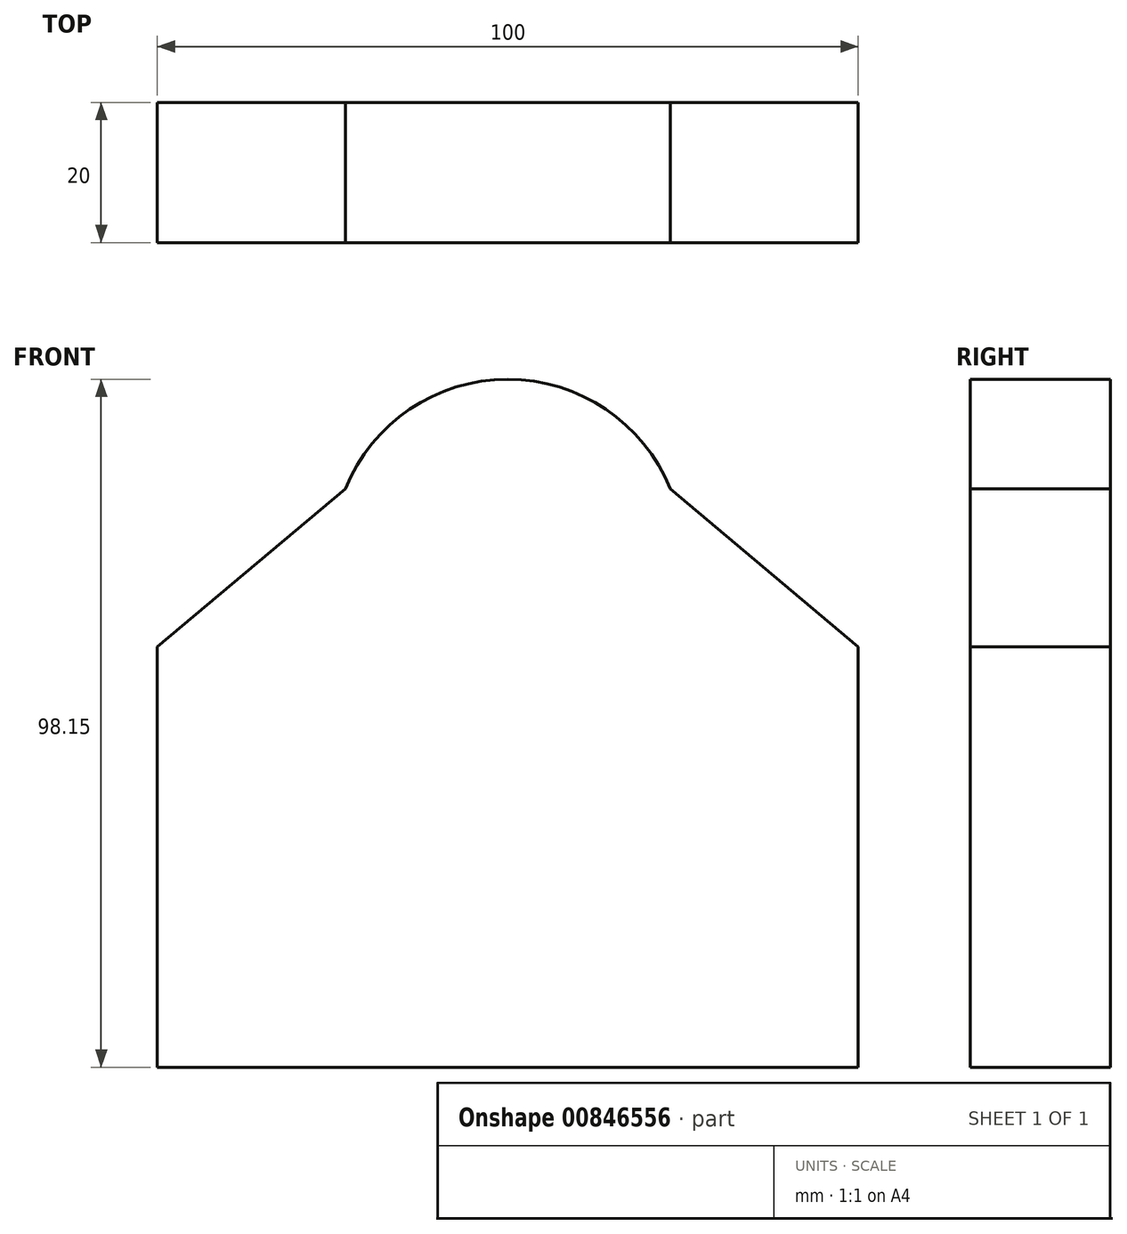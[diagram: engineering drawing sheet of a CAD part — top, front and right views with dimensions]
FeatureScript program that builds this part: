
annotation { "Feature Type Name" : "Feature", "Feature Type Description" : "" }
export const myFeature = defineFeature(function(context is Context, id is Id, definition is map)
    precondition{}
    {
        {
            var Q0;
            Q0=qCreatedBy(makeId("Front.planeOp"),FACE);
            var sketch = newSketch(context, id + "F0", { "sketchPlane" : qUnion([Q0])});
            skLineSegment(sketch, "E0", {"start": v(-52.7, -32.35) * mm, "end": v(47.3, -32.35) * mm});
            skLineSegment(sketch, "E1", {"start": v(-52.7, -32.35) * mm, "end": v(-52.7, 27.65) * mm});
            skLineSegment(sketch, "E2", {"start": v(47.3, 27.65) * mm, "end": v(47.3, -32.35) * mm});
            skLineSegment(sketch, "E3", {"start": v(47.3, 27.65) * mm, "end": v(20.5, 50.15) * mm});
            skLineSegment(sketch, "E4", {"start": v(-52.7, 27.65) * mm, "end": v(-25.88, 50.15) * mm});
            skArc(sketch, "E5", {"start": v(20.5, 50.15) * mm, "mid": v(-2.7, 65.8) * mm, "end": v(-25.88, 50.15) * mm});
            skSolve(sketch);
        }
        {
            var Q0;
            Q0 = qSketchRegion(id + "F0", true);
            extrude(context, id + "F1", {"entities" : qUnion([Q0]), "depth" : 20 * mm, "offsetDistance" : 25 * mm});
        }
    });
